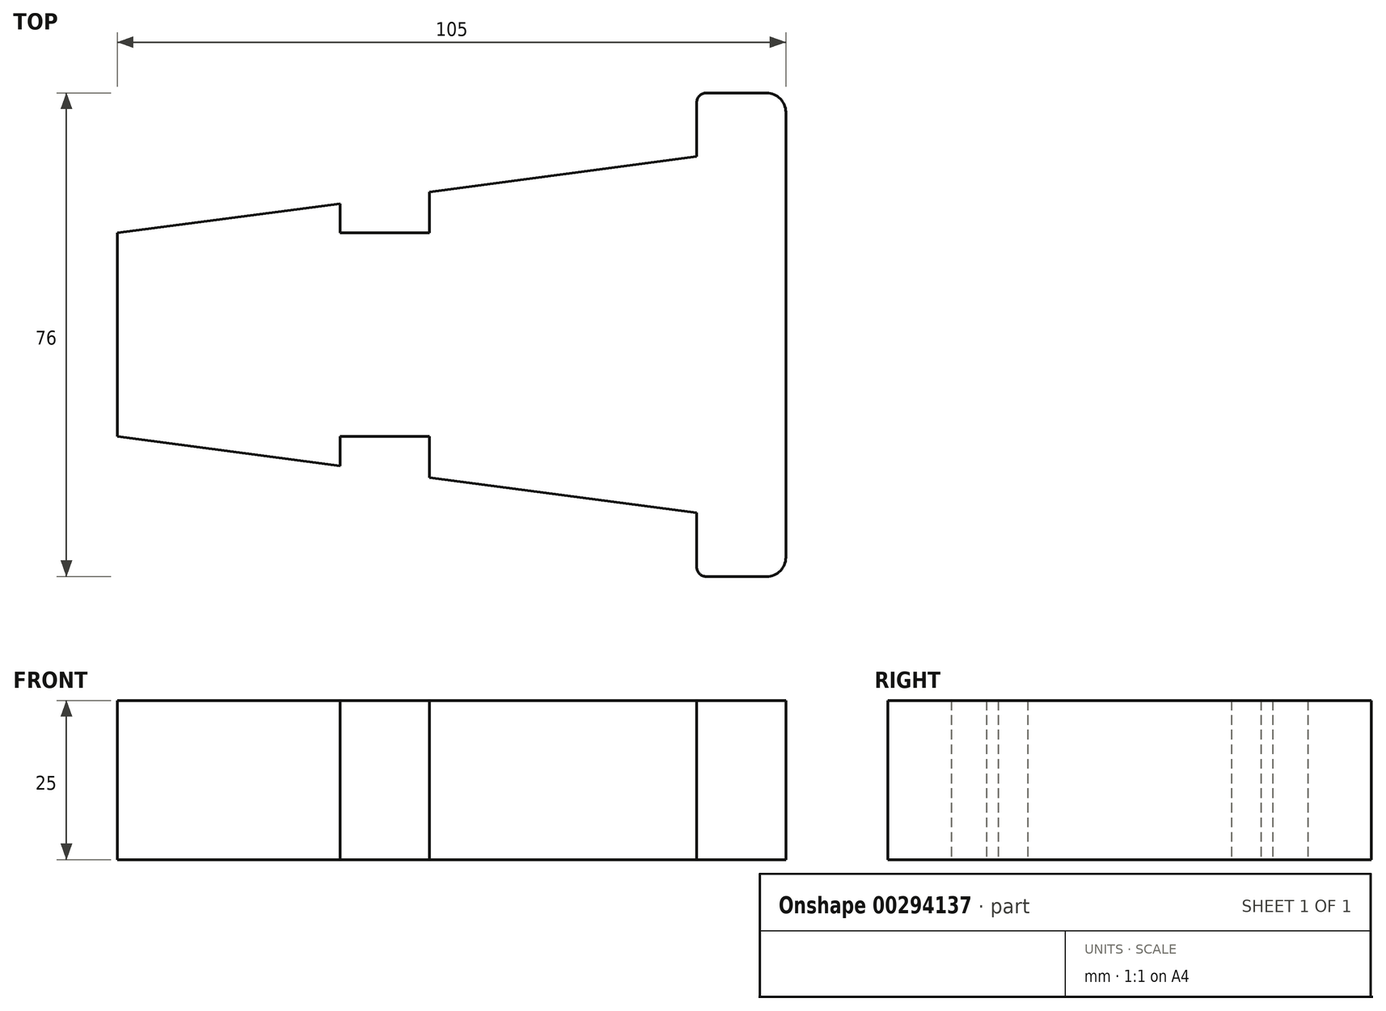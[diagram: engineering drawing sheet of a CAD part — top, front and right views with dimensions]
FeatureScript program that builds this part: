
annotation { "Feature Type Name" : "Feature", "Feature Type Description" : "" }
export const myFeature = defineFeature(function(context is Context, id is Id, definition is map)
    precondition{}
    {
        {
            var Q0;
            Q0=qCreatedBy(makeId("Top.planeOp"),FACE);
            var sketch = newSketch(context, id + "F0", { "sketchPlane" : qUnion([Q0])});
            skLineSegment(sketch, "E0", {"start": v(64, 44.18) * mm, "end": v(64, -25.82) * mm});
            skPoint(sketch, "E1.end.orphan", {"position": v(64, 9.18) * mm});
            skLineSegment(sketch, "E2", {"start": v(-41, 9.18) * mm, "end": v(-41, -6.82) * mm});
            skLineSegment(sketch, "E3", {"start": v(-41, -6.82) * mm, "end": v(-41, 9.18) * mm});
            skLineSegment(sketch, "E4", {"start": v(-41, 9.18) * mm, "end": v(-41, 25.18) * mm});
            skLineSegment(sketch, "E5", {"start": v(-41, 25.18) * mm, "end": v(-41, 9.18) * mm});
            skLineSegment(sketch, "E6", {"start": v(61, 47.18) * mm, "end": v(51.5, 47.18) * mm});
            skLineSegment(sketch, "E7", {"start": v(61, -28.82) * mm, "end": v(51.5, -28.82) * mm});
            skLineSegment(sketch, "E8", {"start": v(50, 45.68) * mm, "end": v(50, 37.18) * mm});
            skLineSegment(sketch, "E9", {"start": v(50, -27.32) * mm, "end": v(50, -18.82) * mm});
            skLineSegment(sketch, "E10", {"start": v(-41, 25.18) * mm, "end": v(-6, 29.8) * mm});
            skLineSegment(sketch, "E11", {"start": v(-41, -6.82) * mm, "end": v(-6, -11.44) * mm});
            skLineSegment(sketch, "E12.trimOffspring", {"start": v(8, -13.28) * mm, "end": v(50, -18.82) * mm});
            skLineSegment(sketch, "E13.trimOffspring", {"start": v(8, 31.64) * mm, "end": v(50, 37.18) * mm});
            skPoint(sketch, "E14.visualSharp", {"position": v(64, 47.18) * mm});
            skArc(sketch, "E14.filletArc", {"start": v(64, 44.18) * mm, "mid": v(63.13, 46.3) * mm, "end": v(61, 47.18) * mm});
            skPoint(sketch, "E15.visualSharp", {"position": v(64, -28.82) * mm});
            skArc(sketch, "E15.filletArc", {"start": v(61, -28.82) * mm, "mid": v(63.13, -27.94) * mm, "end": v(64, -25.82) * mm});
            skPoint(sketch, "E16.visualSharp", {"position": v(50, -28.82) * mm});
            skArc(sketch, "E16.filletArc", {"start": v(50, -27.32) * mm, "mid": v(50.45, -28.38) * mm, "end": v(51.5, -28.82) * mm});
            skPoint(sketch, "E17.visualSharp", {"position": v(50, 47.18) * mm});
            skArc(sketch, "E17.filletArc", {"start": v(51.5, 47.18) * mm, "mid": v(50.45, 46.74) * mm, "end": v(50, 45.68) * mm});
            skLineSegment(sketch, "E18", {"start": v(8, 25.18) * mm, "end": v(8, 31.64) * mm});
            skLineSegment(sketch, "E19", {"start": v(8, -6.82) * mm, "end": v(8, -13.28) * mm});
            skLineSegment(sketch, "E20", {"start": v(8, 25.18) * mm, "end": v(-6, 25.18) * mm});
            skLineSegment(sketch, "E21", {"start": v(-6, 25.18) * mm, "end": v(-6, 29.8) * mm});
            skLineSegment(sketch, "E22", {"start": v(-6, -6.82) * mm, "end": v(8, -6.82) * mm});
            skLineSegment(sketch, "E23", {"start": v(-6, -6.82) * mm, "end": v(-6, -11.44) * mm});
            skSolve(sketch);
        }
        {
            var Q0;
            Q0 = qSketchRegion(id + "F0", true);
            extrude(context, id + "F1", {"entities" : qUnion([Q0]), "depth" : 25 * mm});
        }
    });
